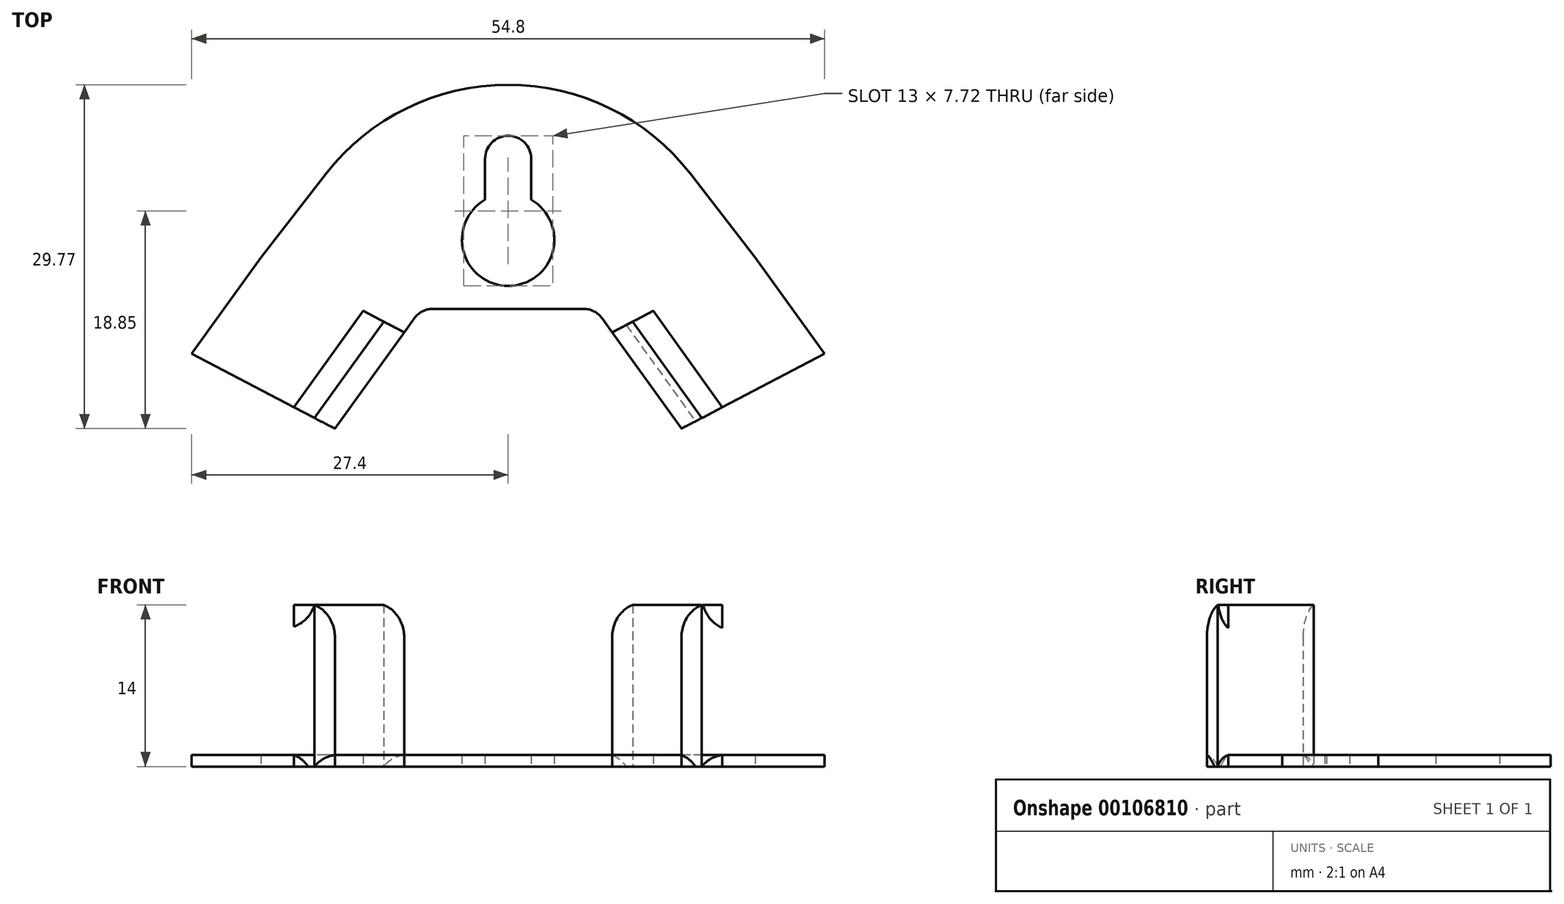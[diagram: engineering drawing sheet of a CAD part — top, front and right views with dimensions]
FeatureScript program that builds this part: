
annotation { "Feature Type Name" : "Feature", "Feature Type Description" : "" }
export const myFeature = defineFeature(function(context is Context, id is Id, definition is map)
    precondition{}
    {
        {
            var Q0;
            Q0=qCreatedBy(makeId("Top.planeOp"),FACE);
            var sketch = newSketch(context, id + "F0", { "sketchPlane" : qUnion([Q0])});
            skLineSegment(sketch, "E0", {"start": v(-15, -8.6) * mm, "end": v(-9, -0.26) * mm});
            skLineSegment(sketch, "E1", {"start": v(-9, -0.26) * mm, "end": v(-8.14, 0.94) * mm});
            skLineSegment(sketch, "E2", {"start": v(15, -8.6) * mm, "end": v(9, -0.26) * mm});
            skLineSegment(sketch, "E3", {"start": v(-27.4, -2.1) * mm, "end": v(-15, -8.6) * mm});
            skLineSegment(sketch, "E4", {"start": v(27.4, -2.1) * mm, "end": v(15, -8.6) * mm});
            skLineSegment(sketch, "E5", {"start": v(21.4, 6.22) * mm, "end": v(9, -0.26) * mm});
            skLineSegment(sketch, "E6", {"start": v(-21.4, 6.22) * mm, "end": v(-9, -0.26) * mm});
            skLineSegment(sketch, "E7", {"start": v(-21.4, 6.22) * mm, "end": v(-27.4, -2.1) * mm});
            skLineSegment(sketch, "E8", {"start": v(27.4, -2.1) * mm, "end": v(21.4, 6.22) * mm});
            skLineSegment(sketch, "E9", {"start": v(-15, -8.6) * mm, "end": v(-16.77, -7.68) * mm});
            skLineSegment(sketch, "E10", {"start": v(-16.77, -7.68) * mm, "end": v(-18.54, -6.75) * mm});
            skLineSegment(sketch, "E11", {"start": v(-9, -0.26) * mm, "end": v(-10.77, 0.66) * mm});
            skLineSegment(sketch, "E12", {"start": v(-10.77, 0.66) * mm, "end": v(-12.55, 1.6) * mm});
            skLineSegment(sketch, "E13", {"start": v(-12.55, 1.6) * mm, "end": v(-18.54, -6.75) * mm});
            skLineSegment(sketch, "E14", {"start": v(-16.77, -7.68) * mm, "end": v(-10.77, 0.66) * mm});
            skLineSegment(sketch, "E15", {"start": v(15, -8.6) * mm, "end": v(16.77, -7.68) * mm});
            skLineSegment(sketch, "E16", {"start": v(16.77, -7.68) * mm, "end": v(18.54, -6.75) * mm});
            skLineSegment(sketch, "E17", {"start": v(9, -0.26) * mm, "end": v(10.77, 0.66) * mm});
            skLineSegment(sketch, "E18", {"start": v(10.77, 0.66) * mm, "end": v(12.55, 1.6) * mm});
            skLineSegment(sketch, "E19", {"start": v(12.55, 1.6) * mm, "end": v(18.54, -6.75) * mm});
            skLineSegment(sketch, "E20", {"start": v(16.77, -7.68) * mm, "end": v(10.77, 0.66) * mm});
            skLineSegment(sketch, "E21", {"start": v(21.4, 6.22) * mm, "end": v(15.79, 13.45) * mm});
            skLineSegment(sketch, "E22", {"start": v(-15.79, 13.45) * mm, "end": v(-21.4, 6.22) * mm});
            skPoint(sketch, "E23.visualSharp", {"position": v(0, 33.75) * mm});
            skArc(sketch, "E23.filletArc", {"start": v(15.79, 13.45) * mm, "mid": v(0, 21.17) * mm, "end": v(-15.79, 13.45) * mm});
            skArc(sketch, "E24", {"start": v(2, 14.75) * mm, "mid": v(0, 16.75) * mm, "end": v(-2, 14.75) * mm});
            skArc(sketch, "E25", {"start": v(-2, 11.21) * mm, "mid": v(0, 3.75) * mm, "end": v(2, 11.21) * mm});
            skLineSegment(sketch, "E26", {"start": v(-2, 14.75) * mm, "end": v(-2, 11.21) * mm});
            skLineSegment(sketch, "E27", {"start": v(2, 14.75) * mm, "end": v(2, 11.21) * mm});
            skLineSegment(sketch, "E28", {"start": v(9, -0.26) * mm, "end": v(8.14, 0.94) * mm});
            skLineSegment(sketch, "E29", {"start": v(6.52, 1.77) * mm, "end": v(-6.52, 1.77) * mm});
            skLineSegment(sketch, "E30.trimOffspring", {"start": v(0, 1.77) * mm, "end": v(0, 1.17) * mm});
            skLineSegment(sketch, "E31.trimOffspring", {"start": v(8.14, 0.94) * mm, "end": v(9, -0.26) * mm});
            skPoint(sketch, "E32.orphan", {"position": v(0, 16.75) * mm});
            skPoint(sketch, "E33.visualSharp", {"position": v(-7.54, 1.77) * mm});
            skArc(sketch, "E33.filletArc", {"start": v(-6.52, 1.77) * mm, "mid": v(-7.43, 1.55) * mm, "end": v(-8.14, 0.94) * mm});
            skPoint(sketch, "E34.visualSharp", {"position": v(7.54, 1.77) * mm});
            skArc(sketch, "E34.filletArc", {"start": v(8.14, 0.94) * mm, "mid": v(7.43, 1.55) * mm, "end": v(6.52, 1.77) * mm});
            skSolve(sketch);
        }
        {
            var Q0;
            Q0=makeQuery(id+"F0.imprint","IMPRINT",FACE,{"disambiguationData":[TD([[makeQuery(id+"F0.imprint","IMPRINT",EDGE,{"derivedFrom":sQuery(id+"F0.wireOp",EDGE,"E0")}),1.0]])]});
            var Q1;
            Q1=makeQuery(id+"F0.imprint","IMPRINT",FACE,{"disambiguationData":[TD([[makeQuery(id+"F0.imprint","IMPRINT",EDGE,{"derivedFrom":sQuery(id+"F0.wireOp",EDGE,"E2")}),-1.0]])]});
            extrude(context, id + "F1", {"entities" : qUnion([Q0, Q1]), "depth" : 14 * mm});
        }
        {
            var Q0;
            Q0=makeQuery(id+"F0.imprint","IMPRINT",FACE,{"disambiguationData":[TD([[makeQuery(id+"F0.imprint","IMPRINT",EDGE,{"derivedFrom":sQuery(id+"F0.wireOp",EDGE,"E10")}),-1.0]])]});
            var Q1;
            Q1=makeQuery(id+"F0.imprint","IMPRINT",FACE,{"disambiguationData":[TD([[makeQuery(id+"F0.imprint","IMPRINT",EDGE,{"derivedFrom":sQuery(id+"F0.wireOp",EDGE,"E16")}),1.0]])]});
            extrude(context, id + "F2", {"entities" : qUnion([Q0, Q1]), "depth" : 14 * mm, "hasSecondDirection" : true, "secondDirectionOppositeDirection" : false, "secondDirectionDepth" : 12 * mm});
        }
        {
            var Q0;
            Q0=makeQuery(id+"F0.imprint","IMPRINT",FACE,{"disambiguationData":[TD([[makeQuery(id+"F0.imprint","IMPRINT",EDGE,{"derivedFrom":sQuery(id+"F0.wireOp",EDGE,"E5")}),-1.0]])]});
            var Q1;
            Q1=makeQuery(id+"F0.imprint","IMPRINT",FACE,{"disambiguationData":[TD([[makeQuery(id+"F0.imprint","IMPRINT",EDGE,{"derivedFrom":sQuery(id+"F0.wireOp",EDGE,"E3")}),1.0]])]});
            var Q2;
            Q2=makeQuery(id+"F0.imprint","IMPRINT",FACE,{"disambiguationData":[TD([[makeQuery(id+"F0.imprint","IMPRINT",EDGE,{"derivedFrom":sQuery(id+"F0.wireOp",EDGE,"E10")}),-1.0]])]});
            var Q3;
            Q3=makeQuery(id+"F0.imprint","IMPRINT",FACE,{"disambiguationData":[TD([[makeQuery(id+"F0.imprint","IMPRINT",EDGE,{"derivedFrom":sQuery(id+"F0.wireOp",EDGE,"E16")}),1.0]])]});
            var Q4;
            Q4=makeQuery(id+"F0.imprint","IMPRINT",FACE,{"disambiguationData":[TD([[makeQuery(id+"F0.imprint","IMPRINT",EDGE,{"derivedFrom":sQuery(id+"F0.wireOp",EDGE,"E4")}),-1.0]])]});
            extrude(context, id + "F3", {"entities" : qUnion([Q0, Q1, Q2, Q3, Q4]), "depth" : 1 * mm});
        }
        {
            var Q0;
            Q0=makeQuery(id+"F3.opExtrude","CAP_EDGE",EDGE,{"disambiguationData":[OSD([sQuery(id+"F0.wireOp",EDGE,"E14")])],"isStart":false});
            var Q1;
            Q1=makeQuery(id+"F1.opExtrude","CAP_EDGE",EDGE,{"disambiguationData":[OSD([sQuery(id+"F0.wireOp",EDGE,"E0")])],"isStart":false});
            var Q2;
            Q2=makeQuery(id+"F1.opExtrude","CAP_EDGE",EDGE,{"disambiguationData":[OSD([sQuery(id+"F0.wireOp",EDGE,"E2")])],"isStart":false});
            var Q3;
            Q3=makeQuery(id+"F3.opExtrude","CAP_EDGE",EDGE,{"disambiguationData":[OSD([sQuery(id+"F0.wireOp",EDGE,"E20")])],"isStart":false});
            fillet(context, id + "F4", {"entities" : qUnion([Q0, Q1, Q2, Q3]), "radius" : 3 * mm, "tangentPropagation" : true, "allowEdgeOverflow" : false});
        }
        {
            var Q0;
            Q0=makeQuery(id+"F2.opExtrude","CAP_EDGE",EDGE,{"disambiguationData":[OSD([sQuery(id+"F0.wireOp",EDGE,"E14")])],"isStart":true});
            var Q1;
            Q1=makeQuery(id+"F2.opExtrude","CAP_EDGE",EDGE,{"disambiguationData":[OSD([sQuery(id+"F0.wireOp",EDGE,"E20")])],"isStart":true});
            fillet(context, id + "F5", {"entities" : qUnion([Q0, Q1]), "radius" : 3 * mm, "tangentPropagation" : true, "allowEdgeOverflow" : false});
        }
    });
